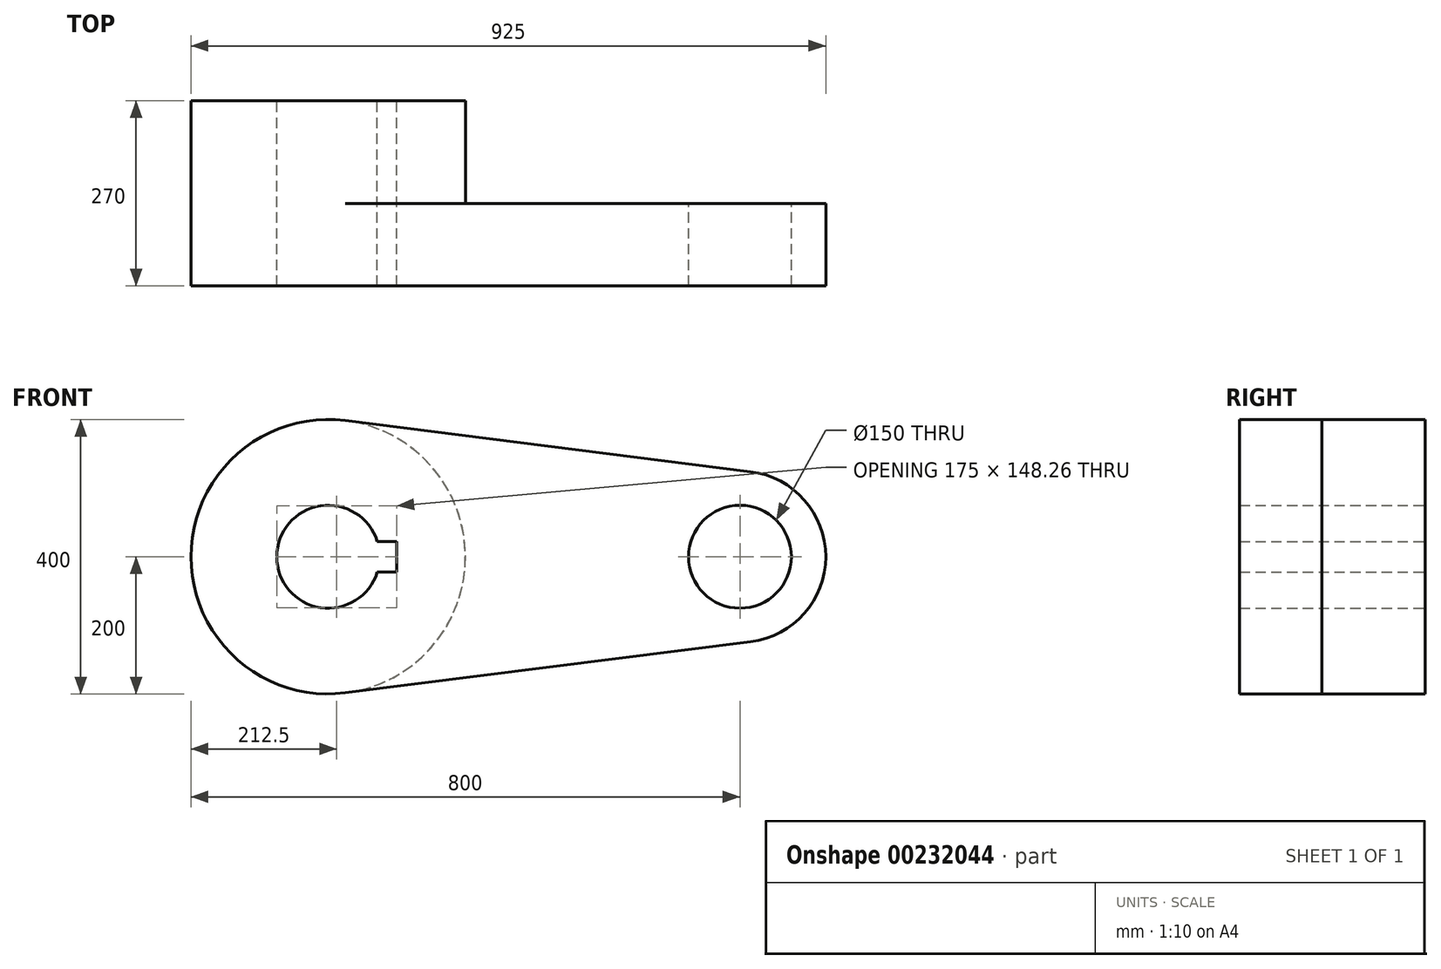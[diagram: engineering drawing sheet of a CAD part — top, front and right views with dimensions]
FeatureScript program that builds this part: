
annotation { "Feature Type Name" : "Feature", "Feature Type Description" : "" }
export const myFeature = defineFeature(function(context is Context, id is Id, definition is map)
    precondition{}
    {
        {
            var Q0;
            Q0=qCreatedBy(makeId("Front.planeOp"),FACE);
            var sketch = newSketch(context, id + "F0", { "sketchPlane" : qUnion([Q0])});
            skCircle(sketch, "E0", {"center": v(0, 0) * mm, "radius": 200 * mm});
            skCircle(sketch, "E1", {"center": v(600, 0) * mm, "radius": 125 * mm});
            skLineSegment(sketch, "E2", {"start": v(25, 198.43) * mm, "end": v(615.63, 124.02) * mm});
            skLineSegment(sketch, "E3", {"start": v(25, -198.43) * mm, "end": v(615.62, -124.02) * mm});
            skCircle(sketch, "E4", {"center": v(0, 0) * mm, "radius": 75 * mm});
            skCircle(sketch, "E5", {"center": v(600, 0) * mm, "radius": 75 * mm});
            skLineSegment(sketch, "E6.bottom", {"start": v(-100, -22.5) * mm, "end": v(100, -22.5) * mm});
            skLineSegment(sketch, "E6.top", {"start": v(-100, 22.5) * mm, "end": v(100, 22.5) * mm});
            skLineSegment(sketch, "E6.left", {"start": v(-100, -22.5) * mm, "end": v(-100, 22.5) * mm});
            skLineSegment(sketch, "E6.right", {"start": v(100, -22.5) * mm, "end": v(100, 22.5) * mm});
            skSolve(sketch);
        }
        {
            var Q0;
            {var subQ11=sQuery(id+"F0.wireOp",EDGE,"E6.left");Q0=makeQuery(id+"F0.imprint","IMPRINT",FACE,{"disambiguationData":[TD([[makeQuery(id+"F0.imprint","IMPRINT",EDGE,{"derivedFrom":subQ11}),1.0]])]});}
            var Q1;
            {var subQ5=sQuery(id+"F0.wireOp",EDGE,"E6.left");Q1=makeQuery(id+"F0.imprint","IMPRINT",FACE,{"disambiguationData":[TD([[makeQuery(id+"F0.imprint","IMPRINT",EDGE,{"derivedFrom":subQ5}),-1.0]])]});}
            var Q2;
            {var subQ0=sQuery(id+"F0.wireOp",EDGE,"E2");Q2=makeQuery(id+"F0.imprint","IMPRINT",FACE,{"disambiguationData":[TD([[makeQuery(id+"F0.imprint","IMPRINT",EDGE,{"derivedFrom":subQ0}),-1.0]])]});}
            var Q3;
            Q3=makeQuery(id+"F0.imprint","IMPRINT",FACE,{"disambiguationData":[TD([[makeQuery(id+"F0.imprint","IMPRINT",EDGE,{"derivedFrom":sQuery(id+"F0.wireOp",EDGE,"E5")}),-1.0]])]});
            extrude(context, id + "F1", {"entities" : qUnion([Q0, Q1, Q2, Q3]), "depth" : 120 * mm});
        }
        {
            var Q0;
            {var subQ11=sQuery(id+"F0.wireOp",EDGE,"E6.left");Q0=makeQuery(id+"F0.imprint","IMPRINT",FACE,{"disambiguationData":[TD([[makeQuery(id+"F0.imprint","IMPRINT",EDGE,{"derivedFrom":subQ11}),1.0]])]});}
            var Q1;
            {var subQ5=sQuery(id+"F0.wireOp",EDGE,"E6.left");Q1=makeQuery(id+"F0.imprint","IMPRINT",FACE,{"disambiguationData":[TD([[makeQuery(id+"F0.imprint","IMPRINT",EDGE,{"derivedFrom":subQ5}),-1.0]])]});}
            extrude(context, id + "F2", {"entities" : qUnion([Q0, Q1]), "operationType" : NewBodyOperationType.ADD, "oppositeDirection" : true, "depth" : 150 * mm});
        }
    });
